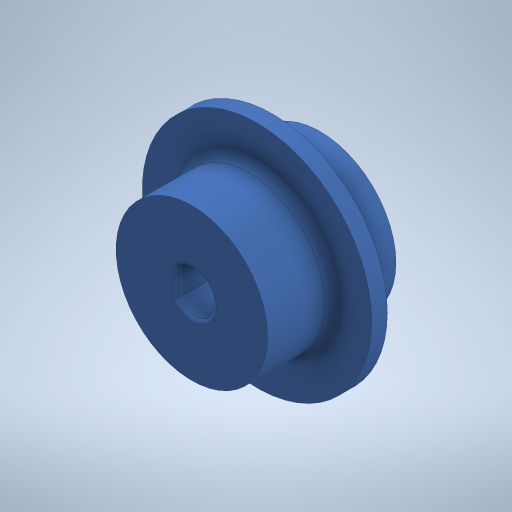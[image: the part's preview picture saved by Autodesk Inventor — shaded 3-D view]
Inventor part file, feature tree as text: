
AUTODESK INVENTOR PART (.ipt)
format: ipt  version: 2024 (Build 280153000, 153)  size: 316,416 bytes
history: native  units: mm
features: fillet x2, revolve x1, extrude x1, sketch x1
ambient origin geometry x8: Origin, YZ Plane, XZ Plane, XY Plane, X Axis, Y Axis, Z Axis, Center Point
bodies: Solid1 (feature_tree)
feature tree (5):
  revolve  "Revolution1"  [1 undecoded]
  extrude  "Extrusion1"  Depth=0.4mm
  fillet  "Fillet1"  Radius=8.15mm
  fillet  "Fillet2"  [1 undecoded]
  sketch  "Sketch2"  dims[d1=7.25mm d2=2.0mm d3=7.5mm d4=8.15mm d5=90.0deg d6=5.2mm d7=2.0mm d8=10.0mm d9=0.0mm d10=14.0mm d11=1.0mm d12=1.9mm d13=7.95mm d14=0.4mm]
note: 2 required parameter values undecoded (feature->parameter linkage not recoverable at this tier; creation-order binding heuristic only, values carry confidence <= 0.55)